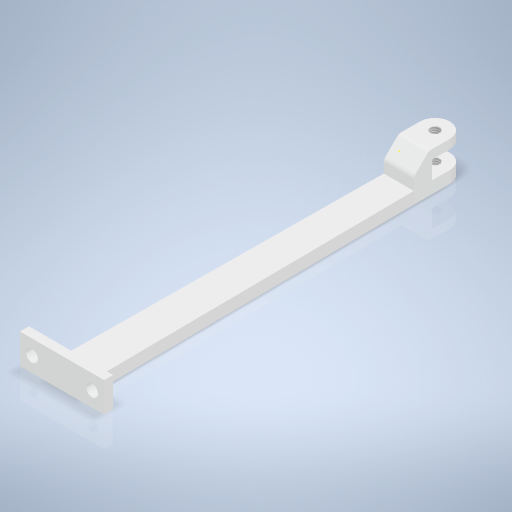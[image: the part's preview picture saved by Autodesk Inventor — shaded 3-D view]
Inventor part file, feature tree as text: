
AUTODESK INVENTOR PART (.ipt)
format: ipt  version: 2024 (Build 280153000, 153)  size: 271,872 bytes
history: native  units: mm
features: other x3, sketch x1
ambient origin geometry x8: Origin, YZ Plane, XZ Plane, XY Plane, X Axis, Y Axis, Z Axis, Center Point
bodies: Volumenkörper1 (feature_tree)
feature tree (4):
  other  "205.ipt"
  other  "Volumenkörper1::205.ipt"
  other  "Bezeichnung1"
  sketch  "Skizze1"  dims[d0=10.0mm]
